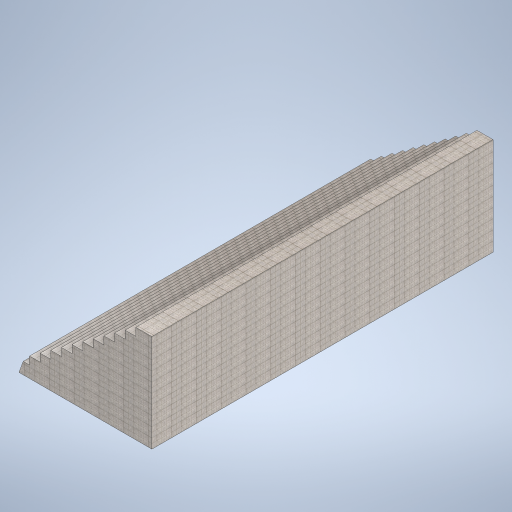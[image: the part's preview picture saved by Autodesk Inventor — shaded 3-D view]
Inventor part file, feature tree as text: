
AUTODESK INVENTOR PART (.ipt)
format: ipt  version: 2024.2 (Build 282272000, 272)  size: 445,952 bytes
history: native  units: mm
features: extrude x3, sketch x3
ambient origin geometry x8: Origin, YZ Plane, XZ Plane, XY Plane, X Axis, Y Axis, Z Axis, Center Point
bodies: Solid1 (feature_tree)
feature tree (6):
  extrude  "Extrusion1"  Depth=7000.0mm
  extrude  "Extrusion2"  Depth=2000.0mm
  extrude  "Extrusion3"  Depth=160.0mm
  sketch  "Sketch1"  dims[d0=2000.0mm d1=7000.0mm]
  sketch  "Sketch2"  dims[d2=2000.0mm d3=0.0mm d4=19.198622mm]
  sketch  "Sketch3"  dims[d5=7000.0mm d6=0.0mm d7=160.0mm d8=160.0mm d9=160.0mm d10=160.0mm d11=160.0mm d12=160.0mm d13=160.0mm d14=160.0mm d15=160.0mm d16=160.0mm d17=160.0mm d18=160.0mm d19=218.0mm d20=218.0mm d21=218.0mm d22=218.0mm d23=218.0mm d24=218.0mm d25=218.0mm d26=218.0mm d27=218.0mm d28=218.0mm d29=218.0mm d30=218.0mm d31=0.0mm d32=0.0mm]
